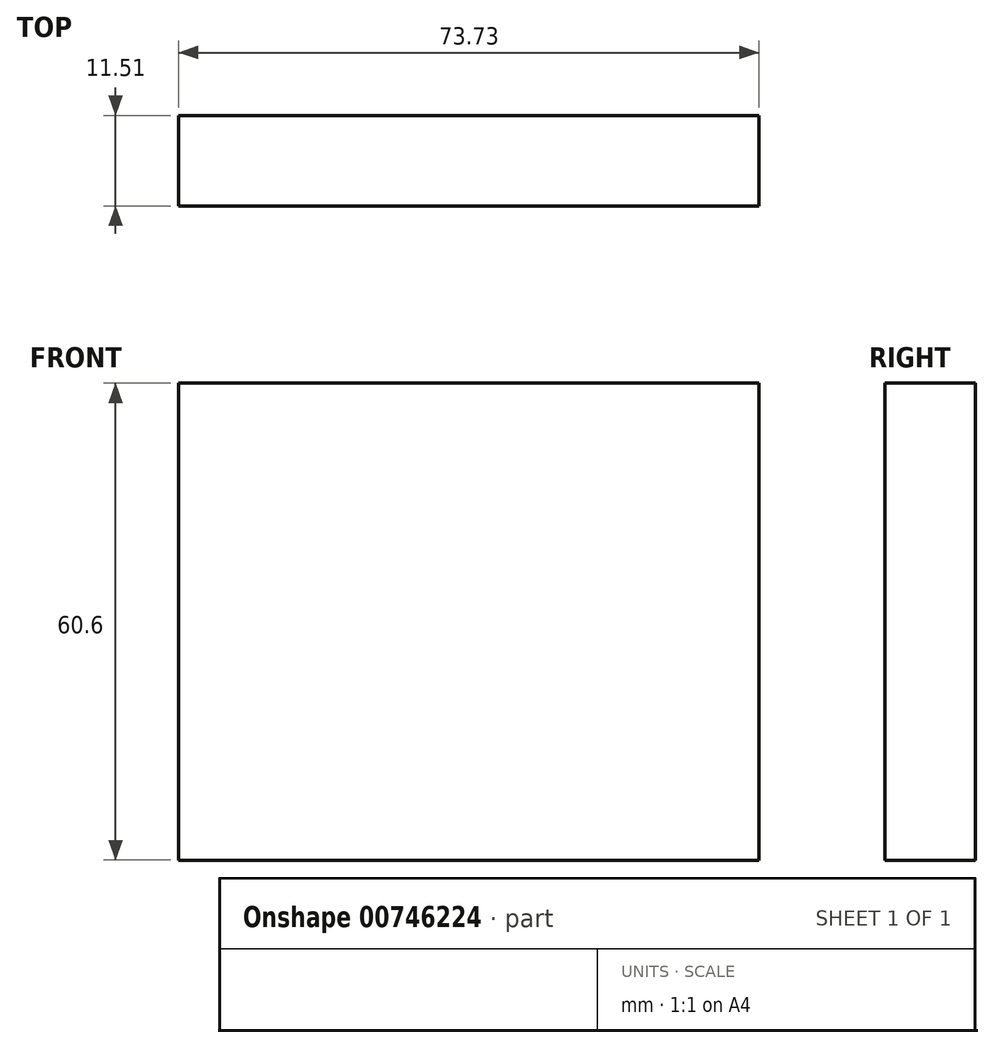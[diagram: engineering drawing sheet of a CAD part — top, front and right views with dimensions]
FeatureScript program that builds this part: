
annotation { "Feature Type Name" : "Feature", "Feature Type Description" : "" }
export const myFeature = defineFeature(function(context is Context, id is Id, definition is map)
    precondition{}
    {
        {
            var Q0;
            Q0=qCreatedBy(makeId("Front.planeOp"),FACE);
            var sketch = newSketch(context, id + "F0", { "sketchPlane" : qUnion([Q0])});
            skLineSegment(sketch, "E0.bottom", {"start": v(-54.59, 25.86) * mm, "end": v(19.14, 25.86) * mm});
            skLineSegment(sketch, "E0.top", {"start": v(-54.59, -34.74) * mm, "end": v(19.14, -34.74) * mm});
            skLineSegment(sketch, "E0.left", {"start": v(-54.59, 25.86) * mm, "end": v(-54.59, -34.74) * mm});
            skLineSegment(sketch, "E0.right", {"start": v(19.14, 25.86) * mm, "end": v(19.14, -34.74) * mm});
            skSolve(sketch);
        }
        {
            var Q0;
            Q0=sQuery(id+"F0.wireOp",EDGE,"E0.left");
            var Q1;
            Q1=sQuery(id+"F0.wireOp",EDGE,"E0.right");
            var Q2;
            Q2=sQuery(id+"F0.wireOp",EDGE,"E0.top");
            var Q3;
            Q3=sQuery(id+"F0.wireOp",EDGE,"E0.bottom");
            extrude(context, id + "F1", {"bodyType" : ToolBodyType.SURFACE, "surfaceEntities" : qUnion([Q0, Q1, Q2, Q3]), "depth" : 11.5 * mm, "offsetDistance" : 25.4 * mm});
        }
    });
